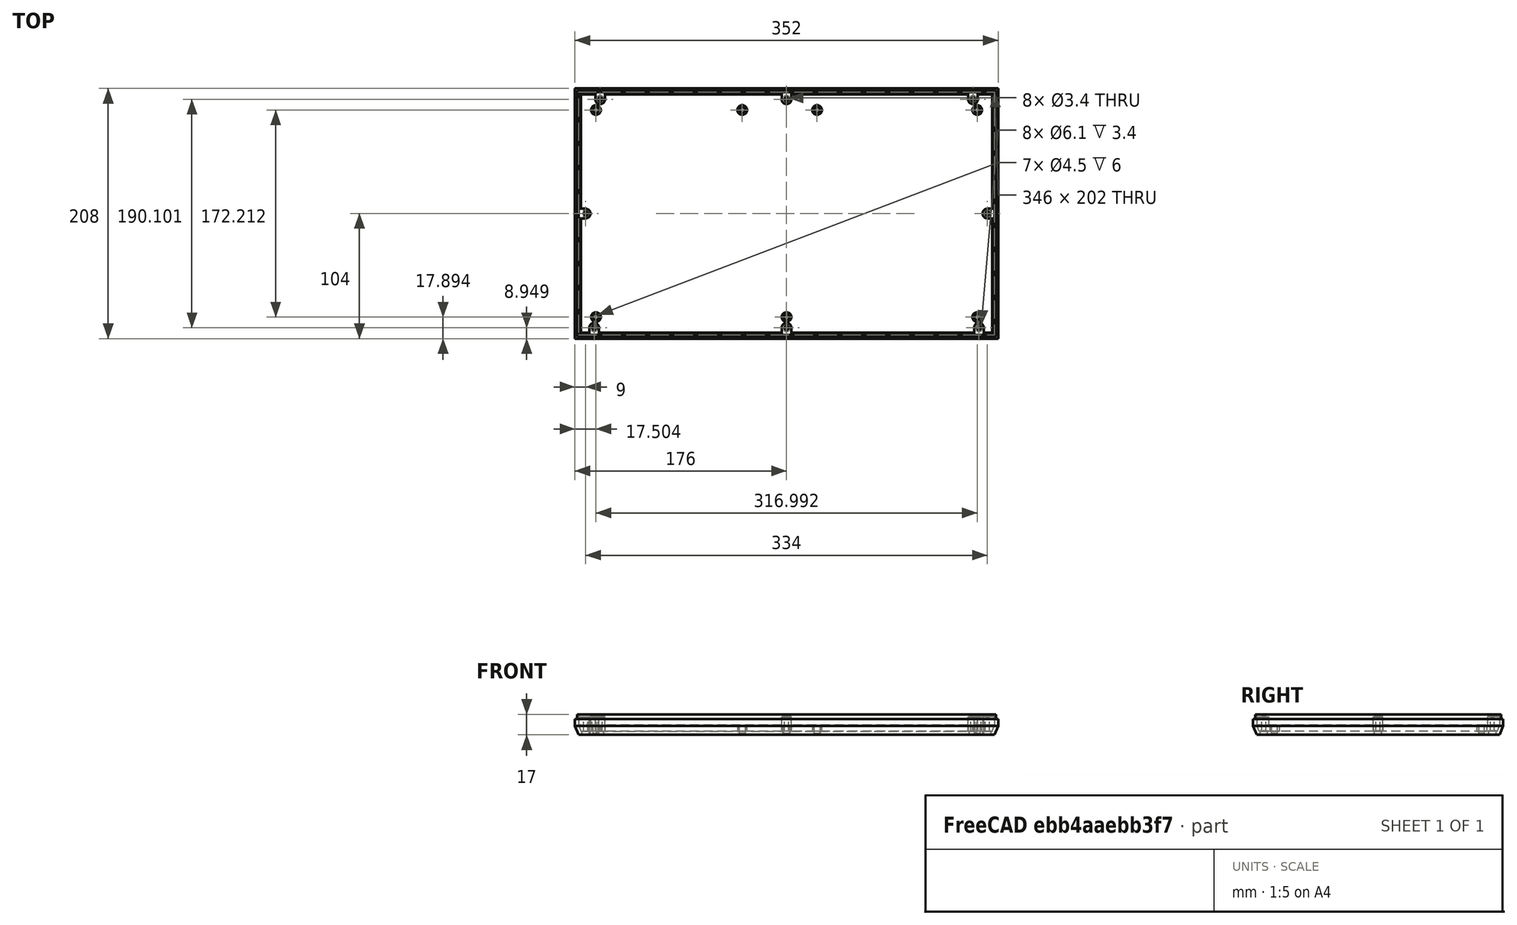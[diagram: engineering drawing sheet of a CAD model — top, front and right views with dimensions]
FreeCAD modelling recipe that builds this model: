
FCSTD DOCUMENT  (FreeCAD 0.21R33771 (Git))
Label: CaseBottom
License: All rights reserved
LicenseURL: https://en.wikipedia.org/wiki/All_rights_reserved
objects: Sketcher::SketchObject×7, PartDesign::Pad×5, PartDesign::Body×2, Mesh::Feature×1, PartDesign::Chamfer×1, PartDesign::Thickness×1, PartDesign::Hole×1, PartDesign::Pocket×1, App::Part×1
note: 27 computed .brp shape members not serialized (recipe doc carries the construction recipe); baked Part::Feature solids carry a one-line shape summary decoded from their .brp

FEATURE [Mesh::Feature] ok240pcb
FEATURE [Sketcher::SketchObject] Sketch  label="Upper001"
  AttachmentOffset = pos=(0,0,6) rot=(0,0,1;0rad)
  FullyConstrained = true
  MapMode = 5
  Placement = pos=(0,0,6) rot=(0,0,1;0rad)
  Support = -> [XY_Plane030]
  sketch-geometry (5):
    g0: LineSegment StartX=-173 StartY=101 StartZ=0 EndX=-173 EndY=-101 EndZ=0
    g1: LineSegment StartX=-173 StartY=-101 StartZ=0 EndX=173 EndY=-101 EndZ=0
    g2: LineSegment StartX=173 StartY=-101 StartZ=0 EndX=173 EndY=101 EndZ=0
    g3: LineSegment StartX=173 StartY=101 StartZ=0 EndX=-173 EndY=101 EndZ=0
    g4: GeomPoint X=0 Y=0 Z=0
  constraints (12):
    c: Coincident(g0,g1)
    c: Coincident(g1,g2)
    c: Coincident(g2,g3)
    c: Coincident(g3,g0)
    c: Horizontal(g1)
    c: Horizontal(g3)
    c: Vertical(g0)
    c: Vertical(g2)
    c: Symmetric(g1,g0,g4)
    c: Coincident(g4,g-1)
    c: DistanceX(g1,g1) = 346
    c: DistanceY(g0,g0) = 202
FEATURE [PartDesign::Pad] Pad
  Direction = (0,0,1)
  Length = 10
  Length2 = 10
  Profile = -> Sketch
  ReferenceAxis = -> Sketch [N_Axis]
  Refine = true
  Reversed = true
  Type = 0
FEATURE [PartDesign::Chamfer] Chamfer
  Angle = 45
  Base = -> Pad [Face6]
  BaseFeature = -> Pad
  ChamferType = 1
  FlipDirection = false
  Refine = true
  Size = 2
  Size2 = 5
  SupportTransform = false
  UseAllEdges = false
FEATURE [PartDesign::Thickness] Thickness001
  Base = -> Chamfer [Face4]
  BaseFeature = -> Chamfer
  Intersection = true
  Join = 1
  Mode = 0
  Refine = true
  SupportTransform = false
  Value = 3
FEATURE [Sketcher::SketchObject] Sketch008  label="Mounts"
  FullyConstrained = false
  MapMode = 5
  Placement = pos=(0,0,-4) rot=(0,0,1;0rad)
  Support = -> [Thickness001]
  sketch-geometry (7):
    g0: Circle CenterX=-158.496 CenterY=86.106 CenterZ=0 NormalX=0 NormalY=0 NormalZ=1 AngleXU=0 Radius=4
    g1: Circle CenterX=-36.83 CenterY=86.106 CenterZ=0 NormalX=0 NormalY=0 NormalZ=1 AngleXU=0 Radius=4
    g2: Circle CenterX=25.4 CenterY=86.106 CenterZ=0 NormalX=0 NormalY=0 NormalZ=1 AngleXU=0 Radius=4
    g3: Circle CenterX=158.496 CenterY=86.106 CenterZ=0 NormalX=0 NormalY=0 NormalZ=1 AngleXU=0 Radius=4
    g4: Circle CenterX=158.496 CenterY=-86.106 CenterZ=0 NormalX=0 NormalY=0 NormalZ=1 AngleXU=0 Radius=4
    g5: Circle CenterX=0.007143 CenterY=-86.106 CenterZ=0 NormalX=0 NormalY=0 NormalZ=1 AngleXU=0 Radius=4
    g6: Circle CenterX=-158.496 CenterY=-86.106 CenterZ=0 NormalX=0 NormalY=0 NormalZ=1 AngleXU=0 Radius=4
  constraints (5):
    c: Block(g0)
    c: Block(g2)
    c: Block(g3)
    c: Block(g4)
    c: Block(g6)
FEATURE [PartDesign::Pad] Pad006  label="MountPads"
  BaseFeature = -> Thickness001
  Direction = (0,0,1)
  Length = 4
  Length2 = 10
  Profile = -> Sketch008
  ReferenceAxis = -> Sketch008 [N_Axis]
  Refine = true
  Type = 0
FEATURE [Sketcher::SketchObject] Sketch010  label="Pillars001"
  ExternalGeometry = -> [Pad006]
  FullyConstrained = true
  MapMode = 5
  Placement = pos=(0,0,-4) rot=(0,0,1;0rad)
  Support = -> [Pad006]
  sketch-geometry (32):
    g0: ArcOfCircle CenterX=-160 CenterY=-95 CenterZ=0 NormalX=0 NormalY=0 NormalZ=1 AngleXU=0 Radius=4 StartAngle=2.5e-07 EndAngle=3.14159
    g1: ArcOfCircle CenterX=-167 CenterY=0 CenterZ=0 NormalX=0 NormalY=0 NormalZ=1 AngleXU=0 Radius=4 StartAngle=4.71239 EndAngle=7.85398
    g2: LineSegment StartX=-164 StartY=-101 StartZ=0 EndX=-164 EndY=-95 EndZ=0
    g3: LineSegment StartX=-156 StartY=-101 StartZ=0 EndX=-156 EndY=-95 EndZ=0
    g4: LineSegment StartX=-156 StartY=-101 StartZ=0 EndX=-164 EndY=-101 EndZ=0
    g5: ArcOfCircle CenterX=-1.50067e-11 CenterY=-95 CenterZ=0 NormalX=0 NormalY=0 NormalZ=1 AngleXU=0 Radius=4 StartAngle=2.5e-07 EndAngle=3.14159
    g6: LineSegment StartX=-4 StartY=-101 StartZ=0 EndX=-4 EndY=-95 EndZ=0
    g7: LineSegment StartX=4 StartY=-101 StartZ=0 EndX=-4 EndY=-101 EndZ=0
    g8: LineSegment StartX=4 StartY=-101 StartZ=0 EndX=4 EndY=-95 EndZ=0
    g9: ArcOfCircle CenterX=160 CenterY=-95 CenterZ=0 NormalX=0 NormalY=0 NormalZ=1 AngleXU=0 Radius=4 StartAngle=2.5e-07 EndAngle=3.14159
    g10: LineSegment StartX=156 StartY=-101 StartZ=0 EndX=156 EndY=-95 EndZ=0
    g11: LineSegment StartX=164 StartY=-101 StartZ=0 EndX=156 EndY=-101 EndZ=0
    g12: LineSegment StartX=164 StartY=-101 StartZ=0 EndX=164 EndY=-95 EndZ=0
    g13: LineSegment StartX=-173 StartY=4 StartZ=0 EndX=-167 EndY=4 EndZ=0
    g14: LineSegment StartX=-173 StartY=4 StartZ=0 EndX=-173 EndY=-4 EndZ=0
    g15: LineSegment StartX=-173 StartY=-4 StartZ=0 EndX=-167 EndY=-4 EndZ=0
    g16: ArcOfCircle CenterX=167 CenterY=0 CenterZ=0 NormalX=0 NormalY=0 NormalZ=1 AngleXU=0 Radius=4 StartAngle=1.5708 EndAngle=4.71239
    g17: LineSegment StartX=173 StartY=4 StartZ=0 EndX=167 EndY=4 EndZ=0
    g18: LineSegment StartX=173 StartY=4 StartZ=0 EndX=173 EndY=-4 EndZ=0
    g19: LineSegment StartX=173 StartY=-4 StartZ=0 EndX=167 EndY=-4 EndZ=0
    g20: ArcOfCircle CenterX=-1.50067e-11 CenterY=95 CenterZ=0 NormalX=0 NormalY=0 NormalZ=1 AngleXU=0 Radius=4 StartAngle=3.14159 EndAngle=6.28319
    g21: LineSegment StartX=-4 StartY=101 StartZ=0 EndX=-4 EndY=95 EndZ=0
    g22: LineSegment StartX=4 StartY=101 StartZ=0 EndX=-4 EndY=101 EndZ=0
    g23: LineSegment StartX=4 StartY=101 StartZ=0 EndX=4 EndY=95 EndZ=0
    g24: ArcOfCircle CenterX=-155 CenterY=95 CenterZ=0 NormalX=0 NormalY=0 NormalZ=1 AngleXU=0 Radius=4 StartAngle=3.14159 EndAngle=6.28319
    g25: LineSegment StartX=-159 StartY=101 StartZ=0 EndX=-159 EndY=95 EndZ=0
    g26: LineSegment StartX=-151 StartY=101 StartZ=0 EndX=-159 EndY=101 EndZ=0
    g27: LineSegment StartX=-151 StartY=101 StartZ=0 EndX=-151 EndY=95 EndZ=0
    g28: ArcOfCircle CenterX=155 CenterY=95 CenterZ=0 NormalX=0 NormalY=0 NormalZ=1 AngleXU=0 Radius=4 StartAngle=3.14159 EndAngle=6.28319
    g29: LineSegment StartX=151 StartY=101 StartZ=0 EndX=151 EndY=95 EndZ=0
    g30: LineSegment StartX=159 StartY=101 StartZ=0 EndX=151 EndY=101 EndZ=0
    g31: LineSegment StartX=159 StartY=101 StartZ=0 EndX=159 EndY=95 EndZ=0
  constraints (77):
    c: PointOnObject(g1,g-1)
    c: PointOnObject(g2,g-3)
    c: Vertical(g2)
    c: PointOnObject(g3,g-3)
    c: Vertical(g3)
    c: Coincident(g4,g3)
    c: Coincident(g4,g2)
    c: DistanceY(g2,g2) = 6
    c: Coincident(g0,g2)
    c: Coincident(g0,g3)
    c: Block(g0)
    c: Vertical(g6)
    c: Vertical(g8)
    c: Coincident(g7,g8)
    c: Coincident(g7,g6)
    c: Equal(g2,g6) = 6
    c: Equal(g8,g6)
    c: Coincident(g5,g6)
    c: Coincident(g5,g8)
    c: Block(g5)
    c: Vertical(g10)
    c: Coincident(g11,g12)
    c: Coincident(g11,g10)
    c: Equal(g12,g10)
    c: Coincident(g9,g10)
    c: Block(g9)
    c: Block(g12)
    c: Coincident(g14,g13)
    c: Vertical(g14)
    c: Coincident(g15,g14)
    c: Coincident(g1,g13)
    c: Coincident(g1,g15)
    c: Radius(g1) = 4
    c: Block(g1)
    c: Parallel(g13,g-1)
    c: Parallel(g15,g-1)
    c: Block(g14)
    c: Coincident(g18,g17)
    c: Vertical(g18)
    c: Coincident(g19,g18)
    c: Coincident(g16,g17)
    c: Coincident(g16,g19)
    c: Radius(g16) = 4
    c: Block(g16)
    c: Block(g18)
    c: Radius(g9) = 4
    c: Radius(g5) = 4
    c: Radius(g0) = 4
    c: Vertical(g21)
    c: Vertical(g23)
    c: Coincident(g22,g23)
    c: Coincident(g22,g21)
    c: Equal(g23,g21)
    c: Coincident(g20,g21)
    c: Coincident(g20,g23)
    c: Block(g20)
    c: Radius(g20) = 4
    c: PointOnObject(g21,g-5)
    c: Vertical(g25)
    c: Vertical(g27)
    c: Coincident(g26,g27)
    c: Coincident(g26,g25)
    c: Equal(g27,g25)
    c: Coincident(g24,g25)
    c: Coincident(g24,g27)
    c: Block(g24)
    c: PointOnObject(g26,g-5)
    c: Vertical(g29)
    c: Vertical(g31)
    c: Coincident(g30,g31)
    c: Coincident(g30,g29)
    c: Equal(g31,g29)
    c: Coincident(g28,g29)
    c: Coincident(g28,g31)
    c: Block(g28)
    c: PointOnObject(g30,g-5)
    c: PointOnObject(g6,g-3)
FEATURE [PartDesign::Pad] Pad007  label="Pillars002"
  BaseFeature = -> Pad006
  Direction = (0,0,1)
  Length = 12
  Length2 = 10
  Profile = -> Sketch010
  ReferenceAxis = -> Sketch010 [N_Axis]
  Refine = true
  Type = 0
FEATURE [Sketcher::SketchObject] Sketch012
  AttachmentOffset = pos=(0,0,6) rot=(0,0,1;0rad)
  FullyConstrained = true
  MapMode = 5
  Placement = pos=(0,0,6) rot=(0,0,1;0rad)
  Support = -> [XY_Plane032]
  sketch-geometry (10):
    g0: LineSegment StartX=173 StartY=-101 StartZ=0 EndX=173 EndY=101 EndZ=0
    g1: LineSegment StartX=173 StartY=101 StartZ=0 EndX=-173 EndY=101 EndZ=0
    g2: LineSegment StartX=-173 StartY=101 StartZ=0 EndX=-173 EndY=-101 EndZ=0
    g3: LineSegment StartX=-173 StartY=-101 StartZ=0 EndX=173 EndY=-101 EndZ=0
    g4: GeomPoint X=0 Y=0 Z=0
    g5: LineSegment StartX=174.3 StartY=-102.3 StartZ=0 EndX=174.3 EndY=102.3 EndZ=0
    g6: LineSegment StartX=174.3 StartY=102.3 StartZ=0 EndX=-174.3 EndY=102.3 EndZ=0
    g7: LineSegment StartX=-174.3 StartY=102.3 StartZ=0 EndX=-174.3 EndY=-102.3 EndZ=0
    g8: LineSegment StartX=-174.3 StartY=-102.3 StartZ=0 EndX=174.3 EndY=-102.3 EndZ=0
    g9: GeomPoint X=0 Y=0 Z=0
  constraints (22):
    c: Coincident(g0,g1)
    c: Coincident(g1,g2)
    c: Coincident(g2,g3)
    c: Coincident(g3,g0)
    c: Horizontal(g1)
    c: Horizontal(g3)
    c: Vertical(g0)
    c: Vertical(g2)
    c: Symmetric(g1,g0,g4)
    c: Coincident(g4,g-1)
    c: Coincident(g5,g6)
    c: Coincident(g6,g7)
    c: Coincident(g7,g8)
    c: Coincident(g8,g5)
    c: Horizontal(g6)
    c: Horizontal(g8)
    c: Vertical(g5)
    c: Vertical(g7)
    c: Symmetric(g6,g5,g9)
    c: Coincident(g9,g4)
    c: Block(g7)
    c: Block(g3)
FEATURE [PartDesign::Pad] Pad008
  Direction = (0,0,1)
  Length = 4
  Length2 = 10
  Profile = -> Sketch012
  ReferenceAxis = -> Sketch012 [N_Axis]
  Refine = true
  Type = 0
FEATURE [PartDesign::Body] Body003  label="Lip"
  Group = -> [Sketch012,Pad008]
  Origin = -> Origin032
  Tip = -> Pad008
FEATURE [Sketcher::SketchObject] Sketch013  label="Holes"
  AttachmentOffset = pos=(0,0,-15) rot=(0,0,1;0rad)
  FullyConstrained = true
  MapMode = 5
  Placement = pos=(0,0,-7) rot=(0,0,1;0rad)
  Support = -> [Pad007]
  sketch-geometry (8):
    g0: Circle CenterX=-155 CenterY=95 CenterZ=0 NormalX=0 NormalY=0 NormalZ=1 AngleXU=0 Radius=1.5462
    g1: Circle CenterX=-167 CenterY=0 CenterZ=0 NormalX=0 NormalY=0 NormalZ=1 AngleXU=0 Radius=1.58365
    g2: Circle CenterX=167 CenterY=0 CenterZ=0 NormalX=0 NormalY=0 NormalZ=1 AngleXU=0 Radius=1.58365
    g3: Circle CenterX=155 CenterY=95 CenterZ=0 NormalX=0 NormalY=0 NormalZ=1 AngleXU=0 Radius=1.5462
    g4: Circle CenterX=-160 CenterY=-95 CenterZ=0 NormalX=0 NormalY=0 NormalZ=1 AngleXU=0 Radius=1.53214
    g5: Circle CenterX=160 CenterY=-95 CenterZ=0 NormalX=0 NormalY=0 NormalZ=1 AngleXU=0 Radius=1.53214
    g6: Circle CenterX=0 CenterY=-95.0507 CenterZ=0 NormalX=0 NormalY=0 NormalZ=1 AngleXU=0 Radius=1.51563
    g7: Circle CenterX=0 CenterY=95.0507 CenterZ=0 NormalX=0 NormalY=0 NormalZ=1 AngleXU=0 Radius=1.51563
  constraints (10):
    c: PointOnObject(g1,g-1)
    c: PointOnObject(g6,g-2)
    c: Block(g0)
    c: Block(g1)
    c: Block(g2)
    c: Block(g3)
    c: Block(g4)
    c: Block(g5)
    c: Block(g6)
    c: Block(g7)
FEATURE [PartDesign::Hole] Hole
  BaseFeature = -> Pad007
  CustomThreadClearance = 0
  Depth = 25
  DepthType = 0
  Diameter = 3.4
  DrillForDepth = false
  DrillPoint = 1
  DrillPointAngle = 115
  HoleCutCountersinkAngle = 90
  HoleCutCustomValues = false
  HoleCutDepth = 3.4
  HoleCutDiameter = 6.1
  HoleCutType = 1
  ModelThread = false
  Profile = -> Sketch013
  Refine = true
  Reversed = true
  Tapered = false
  TaperedAngle = 90
  ThreadClass = 0
  ThreadDepth = 25
  ThreadDepthType = 0
  ThreadDirection = 0
  ThreadFit = 0
  ThreadSize = 9
  ThreadType = 1
  Threaded = false
  UseCustomThreadClearance = false
FEATURE [Sketcher::SketchObject] Sketch014
  FullyConstrained = true
  MapMode = 5
  Placement = pos=(0,0,6) rot=(0,0,1;0rad)
  Support = -> [Hole]
  sketch-geometry (10):
    g0: LineSegment StartX=173 StartY=-101 StartZ=0 EndX=173 EndY=101 EndZ=0
    g1: LineSegment StartX=173 StartY=101 StartZ=0 EndX=-173 EndY=101 EndZ=0
    g2: LineSegment StartX=-173 StartY=101 StartZ=0 EndX=-173 EndY=-101 EndZ=0
    g3: LineSegment StartX=-173 StartY=-101 StartZ=0 EndX=173 EndY=-101 EndZ=0
    g4: GeomPoint X=0 Y=0 Z=0
    g5: LineSegment StartX=174.3 StartY=-102.3 StartZ=0 EndX=174.3 EndY=102.3 EndZ=0
    g6: LineSegment StartX=174.3 StartY=102.3 StartZ=0 EndX=-174.3 EndY=102.3 EndZ=0
    g7: LineSegment StartX=-174.3 StartY=102.3 StartZ=0 EndX=-174.3 EndY=-102.3 EndZ=0
    g8: LineSegment StartX=-174.3 StartY=-102.3 StartZ=0 EndX=174.3 EndY=-102.3 EndZ=0
    g9: GeomPoint X=0 Y=0 Z=0
  constraints (22):
    c: Coincident(g0,g1)
    c: Coincident(g1,g2)
    c: Coincident(g2,g3)
    c: Coincident(g3,g0)
    c: Horizontal(g1)
    c: Horizontal(g3)
    c: Vertical(g0)
    c: Vertical(g2)
    c: Symmetric(g1,g0,g4)
    c: Coincident(g4,g-1)
    c: Coincident(g5,g6)
    c: Coincident(g6,g7)
    c: Coincident(g7,g8)
    c: Coincident(g8,g5)
    c: Horizontal(g6)
    c: Horizontal(g8)
    c: Vertical(g5)
    c: Vertical(g7)
    c: Symmetric(g6,g5,g9)
    c: Coincident(g9,g4)
    c: Block(g1)
    c: Block(g6)
FEATURE [PartDesign::Pad] Pad009
  BaseFeature = -> Hole
  Direction = (0,0,1)
  Length = 4
  Length2 = 10
  Profile = -> Sketch014
  ReferenceAxis = -> Sketch014 [N_Axis]
  Refine = true
  Type = 0
FEATURE [Sketcher::SketchObject] Sketch015  label="PCBMountHoles"
  ExternalGeometry = -> [Pad009]
  FullyConstrained = true
  MapMode = 5
  Support = -> [Pad009]
  sketch-geometry (7):
    g0: Circle CenterX=-158.496 CenterY=-86.106 CenterZ=0 NormalX=0 NormalY=0 NormalZ=1 AngleXU=0 Radius=2.25
    g1: Circle CenterX=0.007143 CenterY=-86.106 CenterZ=0 NormalX=0 NormalY=0 NormalZ=1 AngleXU=0 Radius=2.25
    g2: Circle CenterX=158.496 CenterY=-86.106 CenterZ=0 NormalX=0 NormalY=0 NormalZ=1 AngleXU=0 Radius=2.25
    g3: Circle CenterX=-158.496 CenterY=86.106 CenterZ=0 NormalX=0 NormalY=0 NormalZ=1 AngleXU=0 Radius=2.25
    g4: Circle CenterX=-36.83 CenterY=86.106 CenterZ=0 NormalX=0 NormalY=0 NormalZ=1 AngleXU=0 Radius=2.25
    g5: Circle CenterX=25.4 CenterY=86.106 CenterZ=0 NormalX=0 NormalY=0 NormalZ=1 AngleXU=0 Radius=2.25
    g6: Circle CenterX=158.496 CenterY=86.106 CenterZ=0 NormalX=0 NormalY=0 NormalZ=1 AngleXU=0 Radius=2.25
  constraints (14):
    c: Coincident(g0,g-9)
    c: Coincident(g1,g-8)
    c: Coincident(g2,g-7)
    c: Coincident(g3,g-3)
    c: Coincident(g4,g-4)
    c: Coincident(g5,g-5)
    c: Coincident(g6,g-6)
    c: Equal(g3,g4)
    c: Equal(g3,g5)
    c: Equal(g3,g6)
    c: Equal(g3,g2)
    c: Equal(g3,g1)
    c: Equal(g3,g0)
    c: Diameter(g3) = 4.5
FEATURE [PartDesign::Pocket] Pocket  label="PCBMountHoles001"
  BaseFeature = -> Pad009
  Direction = (0,0,-1)
  Length = 6
  Length2 = 5
  Profile = -> Sketch015
  ReferenceAxis = -> Sketch015 [N_Axis]
  Refine = true
  Type = 0
FEATURE [PartDesign::Body] Body002  label="BottomLid1"
  Group = -> [Sketch,Pad,Chamfer,Thickness001,Sketch008,Pad006,Sketch010,Pad007,Sketch013,Hole,Sketch014,Pad009,Sketch015,Pocket]
  Origin = -> Origin030
  Tip = -> Pocket
FEATURE [App::Part] Part
  Group = -> [Body002,Body003]
  Origin = -> Origin028
